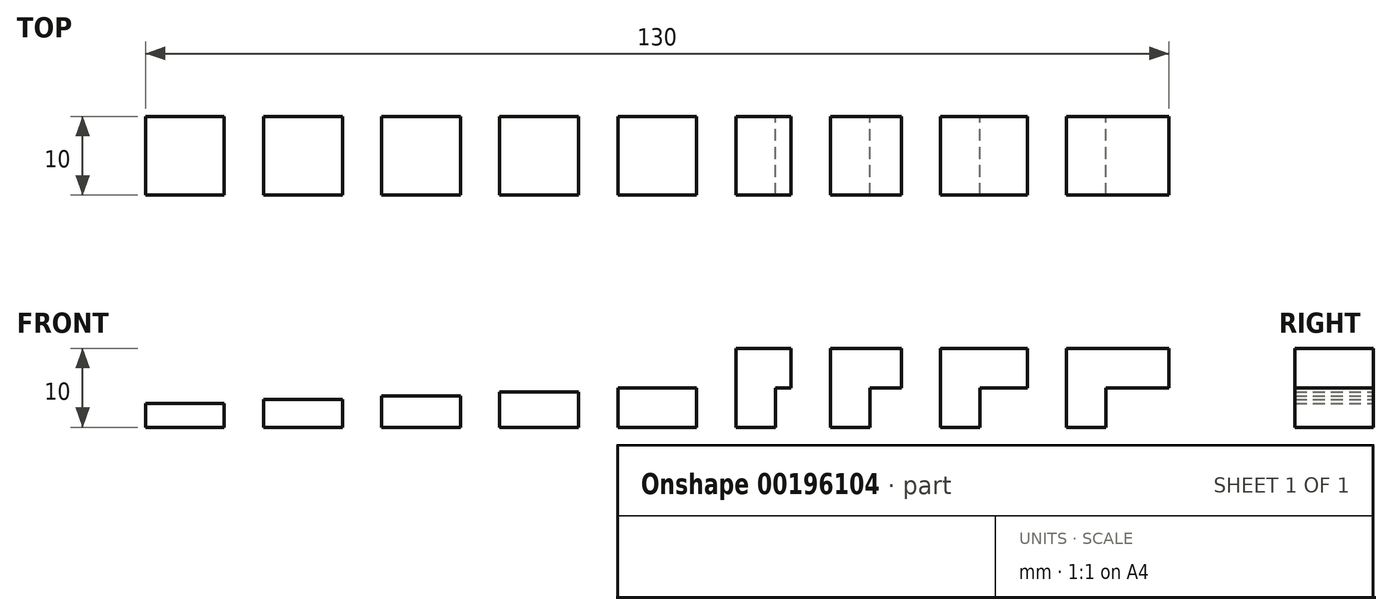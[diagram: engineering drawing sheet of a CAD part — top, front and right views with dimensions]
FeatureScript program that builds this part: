
annotation { "Feature Type Name" : "Feature", "Feature Type Description" : "" }
export const myFeature = defineFeature(function(context is Context, id is Id, definition is map)
    precondition{}
    {
        {
            var Q0;
            Q0=qCreatedBy(makeId("Front.planeOp"),FACE);
            var sketch = newSketch(context, id + "F0", { "sketchPlane" : qUnion([Q0])});
            skLineSegment(sketch, "E0", {"start": v(0, 0) * mm, "end": v(0, 10) * mm});
            skLineSegment(sketch, "E1", {"start": v(0, 10) * mm, "end": v(7, 10) * mm});
            skLineSegment(sketch, "E2", {"start": v(7, 10) * mm, "end": v(7, 5) * mm});
            skLineSegment(sketch, "E3", {"start": v(7, 5) * mm, "end": v(5, 5) * mm});
            skLineSegment(sketch, "E4", {"start": v(5, 5) * mm, "end": v(5, 0) * mm});
            skLineSegment(sketch, "E5", {"start": v(5, 0) * mm, "end": v(0, 0) * mm});
            skLineSegment(sketch, "E6", {"start": v(12, 0) * mm, "end": v(12, 10) * mm});
            skLineSegment(sketch, "E7", {"start": v(12, 10) * mm, "end": v(21, 10) * mm});
            skLineSegment(sketch, "E8", {"start": v(21, 10) * mm, "end": v(21, 5) * mm});
            skLineSegment(sketch, "E9", {"start": v(21, 5) * mm, "end": v(17, 5) * mm});
            skLineSegment(sketch, "E10", {"start": v(17, 5) * mm, "end": v(17, 0) * mm});
            skLineSegment(sketch, "E11", {"start": v(17, 0) * mm, "end": v(12, 0) * mm});
            skLineSegment(sketch, "E12", {"start": v(26, 0) * mm, "end": v(26, 10) * mm});
            skLineSegment(sketch, "E13", {"start": v(26, 10) * mm, "end": v(37, 10) * mm});
            skLineSegment(sketch, "E14", {"start": v(37, 10) * mm, "end": v(37, 5) * mm});
            skLineSegment(sketch, "E15", {"start": v(37, 5) * mm, "end": v(31, 5) * mm});
            skLineSegment(sketch, "E16", {"start": v(31, 5) * mm, "end": v(31, 0) * mm});
            skLineSegment(sketch, "E17", {"start": v(31, 0) * mm, "end": v(26, 0) * mm});
            skLineSegment(sketch, "E18", {"start": v(42, 0) * mm, "end": v(42, 10) * mm});
            skLineSegment(sketch, "E19", {"start": v(55, 10) * mm, "end": v(55, 5) * mm});
            skLineSegment(sketch, "E20", {"start": v(47, 5) * mm, "end": v(47, 0) * mm});
            skLineSegment(sketch, "E21", {"start": v(47, 0) * mm, "end": v(42, 0) * mm});
            skLineSegment(sketch, "E22", {"start": v(42, 10) * mm, "end": v(55, 10) * mm});
            skLineSegment(sketch, "E23", {"start": v(47, 5) * mm, "end": v(55, 5) * mm});
            skSolve(sketch);
        }
        {
            var Q0;
            Q0=makeQuery(id+"F0.imprint","IMPRINT",FACE,{"disambiguationData":[TD([[makeQuery(id+"F0.imprint","IMPRINT",EDGE,{"derivedFrom":sQuery(id+"F0.wireOp",EDGE,"E0")}),-1.0]])]});
            var Q1;
            Q1=makeQuery(id+"F0.imprint","IMPRINT",FACE,{"disambiguationData":[TD([[makeQuery(id+"F0.imprint","IMPRINT",EDGE,{"derivedFrom":sQuery(id+"F0.wireOp",EDGE,"E6")}),-1.0]])]});
            var Q2;
            Q2=makeQuery(id+"F0.imprint","IMPRINT",FACE,{"disambiguationData":[TD([[makeQuery(id+"F0.imprint","IMPRINT",EDGE,{"derivedFrom":sQuery(id+"F0.wireOp",EDGE,"E12")}),-1.0]])]});
            var Q3;
            Q3=makeQuery(id+"F0.imprint","IMPRINT",FACE,{"disambiguationData":[TD([[makeQuery(id+"F0.imprint","IMPRINT",EDGE,{"derivedFrom":sQuery(id+"F0.wireOp",EDGE,"E18")}),-1.0]])]});
            extrude(context, id + "F1", {"entities" : qUnion([Q0, Q1, Q2, Q3]), "depth" : 10 * mm});
        }
        {
            var Q0;
            Q0=qCreatedBy(makeId("Front.planeOp"),FACE);
            var sketch = newSketch(context, id + "F2", { "sketchPlane" : qUnion([Q0])});
            skLineSegment(sketch, "E24.bottom", {"start": v(-60, 3.5) * mm, "end": v(-50, 3.5) * mm});
            skLineSegment(sketch, "E24.top", {"start": v(-60, 0) * mm, "end": v(-50, 0) * mm});
            skLineSegment(sketch, "E24.left", {"start": v(-60, 3.5) * mm, "end": v(-60, 0) * mm});
            skLineSegment(sketch, "E24.right", {"start": v(-50, 3.5) * mm, "end": v(-50, 0) * mm});
            skLineSegment(sketch, "E25.bottom", {"start": v(-45, 4) * mm, "end": v(-35, 4) * mm});
            skLineSegment(sketch, "E25.top", {"start": v(-45, 0) * mm, "end": v(-35, 0) * mm});
            skLineSegment(sketch, "E25.left", {"start": v(-45, 4) * mm, "end": v(-45, 0) * mm});
            skLineSegment(sketch, "E25.right", {"start": v(-35, 4) * mm, "end": v(-35, 0) * mm});
            skLineSegment(sketch, "E26.bottom", {"start": v(-30, 4.5) * mm, "end": v(-20, 4.5) * mm});
            skLineSegment(sketch, "E26.top", {"start": v(-30, 0) * mm, "end": v(-20, 0) * mm});
            skLineSegment(sketch, "E26.left", {"start": v(-30, 4.5) * mm, "end": v(-30, 0) * mm});
            skLineSegment(sketch, "E26.right", {"start": v(-20, 4.5) * mm, "end": v(-20, 0) * mm});
            skLineSegment(sketch, "E27.bottom", {"start": v(-75, 3) * mm, "end": v(-65, 3) * mm});
            skLineSegment(sketch, "E27.top", {"start": v(-75, 0) * mm, "end": v(-65, 0) * mm});
            skLineSegment(sketch, "E27.left", {"start": v(-75, 3) * mm, "end": v(-75, 0) * mm});
            skLineSegment(sketch, "E27.right", {"start": v(-65, 3) * mm, "end": v(-65, 0) * mm});
            skLineSegment(sketch, "E28.bottom", {"start": v(-15, 5) * mm, "end": v(-5, 5) * mm});
            skLineSegment(sketch, "E28.top", {"start": v(-15, 0) * mm, "end": v(-5, 0) * mm});
            skLineSegment(sketch, "E28.left", {"start": v(-15, 5) * mm, "end": v(-15, 0) * mm});
            skLineSegment(sketch, "E28.right", {"start": v(-5, 5) * mm, "end": v(-5, 0) * mm});
            skLineSegment(sketch, "E29", {"start": v(-65, 0) * mm, "end": v(-60, 0) * mm, "construction": true});
            skLineSegment(sketch, "E30", {"start": v(-50, 0) * mm, "end": v(-45, 0) * mm, "construction": true});
            skLineSegment(sketch, "E31", {"start": v(-35, 0) * mm, "end": v(-30, 0) * mm, "construction": true});
            skLineSegment(sketch, "E32", {"start": v(-20, 0) * mm, "end": v(-15, 0) * mm, "construction": true});
            skLineSegment(sketch, "E33", {"start": v(-5, 0) * mm, "end": v(0, 0) * mm, "construction": true});
            skSolve(sketch);
        }
        {
            var Q0;
            Q0=makeQuery(id+"F2.imprint","IMPRINT",FACE,{"disambiguationData":[TD([[makeQuery(id+"F2.imprint","IMPRINT",EDGE,{"derivedFrom":sQuery(id+"F2.wireOp",EDGE,"E27.bottom")}),-1.0]])]});
            var Q1;
            Q1=makeQuery(id+"F2.imprint","IMPRINT",FACE,{"disambiguationData":[TD([[makeQuery(id+"F2.imprint","IMPRINT",EDGE,{"derivedFrom":sQuery(id+"F2.wireOp",EDGE,"E24.bottom")}),-1.0]])]});
            var Q2;
            Q2=makeQuery(id+"F2.imprint","IMPRINT",FACE,{"disambiguationData":[TD([[makeQuery(id+"F2.imprint","IMPRINT",EDGE,{"derivedFrom":sQuery(id+"F2.wireOp",EDGE,"E25.bottom")}),-1.0]])]});
            var Q3;
            Q3=makeQuery(id+"F2.imprint","IMPRINT",FACE,{"disambiguationData":[TD([[makeQuery(id+"F2.imprint","IMPRINT",EDGE,{"derivedFrom":sQuery(id+"F2.wireOp",EDGE,"E26.bottom")}),-1.0]])]});
            var Q4;
            Q4=makeQuery(id+"F2.imprint","IMPRINT",FACE,{"disambiguationData":[TD([[makeQuery(id+"F2.imprint","IMPRINT",EDGE,{"derivedFrom":sQuery(id+"F2.wireOp",EDGE,"E28.bottom")}),-1.0]])]});
            extrude(context, id + "F3", {"entities" : qUnion([Q0, Q1, Q2, Q3, Q4]), "depth" : 10 * mm});
        }
    });
